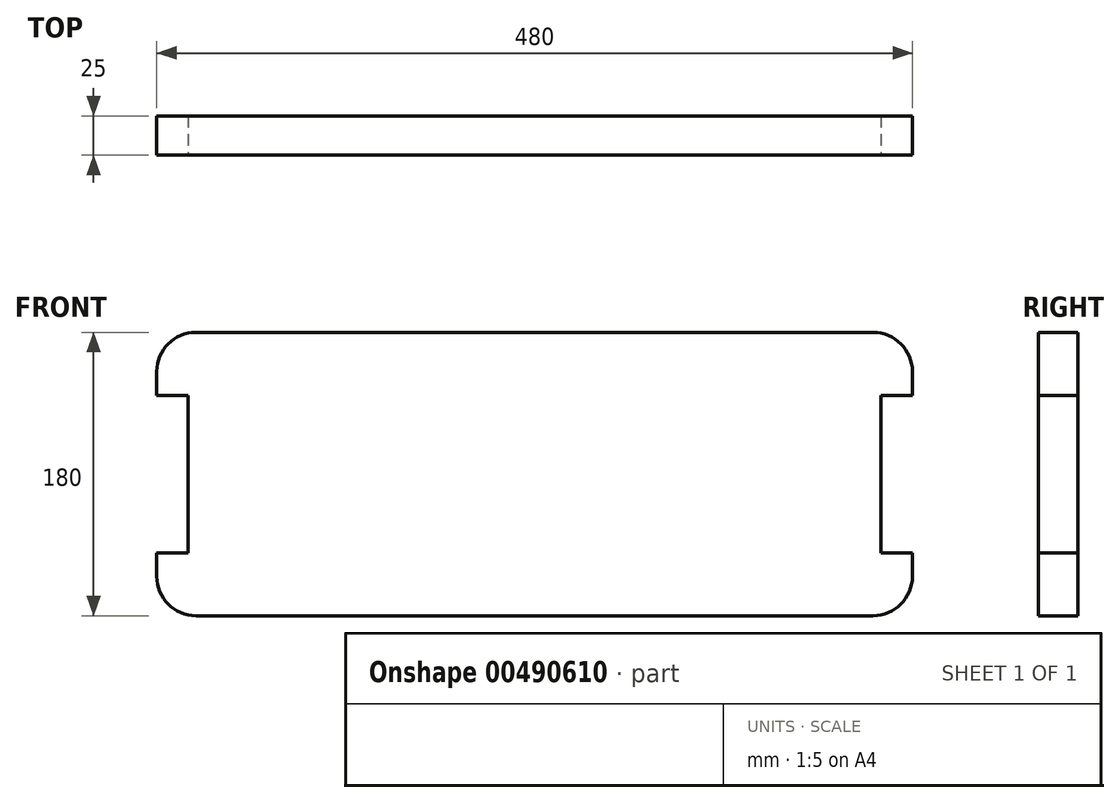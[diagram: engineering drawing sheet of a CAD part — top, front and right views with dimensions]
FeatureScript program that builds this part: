
annotation { "Feature Type Name" : "Feature", "Feature Type Description" : "" }
export const myFeature = defineFeature(function(context is Context, id is Id, definition is map)
    precondition{}
    {
        {
            var Q0;
            Q0=qCreatedBy(makeId("Front.planeOp"),FACE);
            var sketch = newSketch(context, id + "F0", { "sketchPlane" : qUnion([Q0])});
            skLineSegment(sketch, "E0.bottom", {"start": v(-215, 90) * mm, "end": v(215, 90) * mm});
            skLineSegment(sketch, "E0.top", {"start": v(-215, -90) * mm, "end": v(215, -90) * mm});
            skLineSegment(sketch, "E0.left", {"start": v(-240, 65) * mm, "end": v(-240, -65) * mm});
            skLineSegment(sketch, "E0.right", {"start": v(240, 65) * mm, "end": v(240, -65) * mm});
            skPoint(sketch, "E0.middle", {"position": v(0, 0) * mm});
            skPoint(sketch, "E1.visualSharp", {"position": v(-240, -90) * mm});
            skArc(sketch, "E1.filletArc", {"start": v(-240, -65) * mm, "mid": v(-232.68, -82.68) * mm, "end": v(-215, -90) * mm});
            skPoint(sketch, "E2.visualSharp", {"position": v(240, -90) * mm});
            skArc(sketch, "E2.filletArc", {"start": v(215, -90) * mm, "mid": v(232.68, -82.68) * mm, "end": v(240, -65) * mm});
            skPoint(sketch, "E3.visualSharp", {"position": v(240, 90) * mm});
            skArc(sketch, "E3.filletArc", {"start": v(240, 65) * mm, "mid": v(232.68, 82.68) * mm, "end": v(215, 90) * mm});
            skPoint(sketch, "E4.visualSharp", {"position": v(-240, 90) * mm});
            skArc(sketch, "E4.filletArc", {"start": v(-215, 90) * mm, "mid": v(-232.68, 82.68) * mm, "end": v(-240, 65) * mm});
            skSolve(sketch);
        }
        {
            var Q0;
            Q0=qCreatedBy(makeId("Front.planeOp"),FACE);
            var sketch = newSketch(context, id + "F1", { "sketchPlane" : qUnion([Q0])});
            skLineSegment(sketch, "E5.bottom", {"start": v(-220, -50) * mm, "end": v(-240, -50) * mm});
            skLineSegment(sketch, "E5.top", {"start": v(-220, 50) * mm, "end": v(-240, 50) * mm});
            skLineSegment(sketch, "E5.left", {"start": v(-220, -50) * mm, "end": v(-220, 50) * mm});
            skLineSegment(sketch, "E5.right", {"start": v(-240, -50) * mm, "end": v(-240, 50) * mm});
            skPoint(sketch, "E5.middle", {"position": v(-230, 0) * mm});
            skLineSegment(sketch, "E6.MirrorCS", {"start": v(220, -50) * mm, "end": v(240, -50) * mm});
            skPoint(sketch, "E7.MirrorP", {"position": v(230, 0) * mm});
            skLineSegment(sketch, "E8.MirrorCS", {"start": v(240, -50) * mm, "end": v(240, 50) * mm});
            skLineSegment(sketch, "E9.MirrorCS", {"start": v(220, -50) * mm, "end": v(220, 50) * mm});
            skLineSegment(sketch, "E10.MirrorCS", {"start": v(220, 50) * mm, "end": v(240, 50) * mm});
            skSolve(sketch);
        }
        {
            var Q0;
            Q0=makeQuery(id+"F0.imprint","IMPRINT",FACE,{"disambiguationData":[TD([[makeQuery(id+"F0.imprint","IMPRINT",EDGE,{"derivedFrom":sQuery(id+"F0.wireOp",EDGE,"E0.bottom")}),-1.0]])]});
            extrude(context, id + "F2", {"entities" : qUnion([Q0]), "oppositeDirection" : true, "depth" : 25 * mm, "offsetDistance" : 25 * mm});
        }
        {
            var Q0;
            Q0=makeQuery(id+"F1.imprint","IMPRINT",FACE,{"disambiguationData":[TD([[makeQuery(id+"F1.imprint","IMPRINT",EDGE,{"derivedFrom":sQuery(id+"F1.wireOp",EDGE,"E5.bottom")}),-1.0]])]});
            var Q1;
            Q1=makeQuery(id+"F1.imprint","IMPRINT",FACE,{"disambiguationData":[TD([[makeQuery(id+"F1.imprint","IMPRINT",EDGE,{"derivedFrom":sQuery(id+"F1.wireOp",EDGE,"E6.MirrorCS")}),1.0]])]});
            extrude(context, id + "F3", {"entities" : qUnion([Q0, Q1]), "operationType" : NewBodyOperationType.REMOVE, "endBound" : BoundingType.THROUGH_ALL, "oppositeDirection" : true, "depth" : 25 * mm, "offsetDistance" : 25 * mm});
        }
    });
